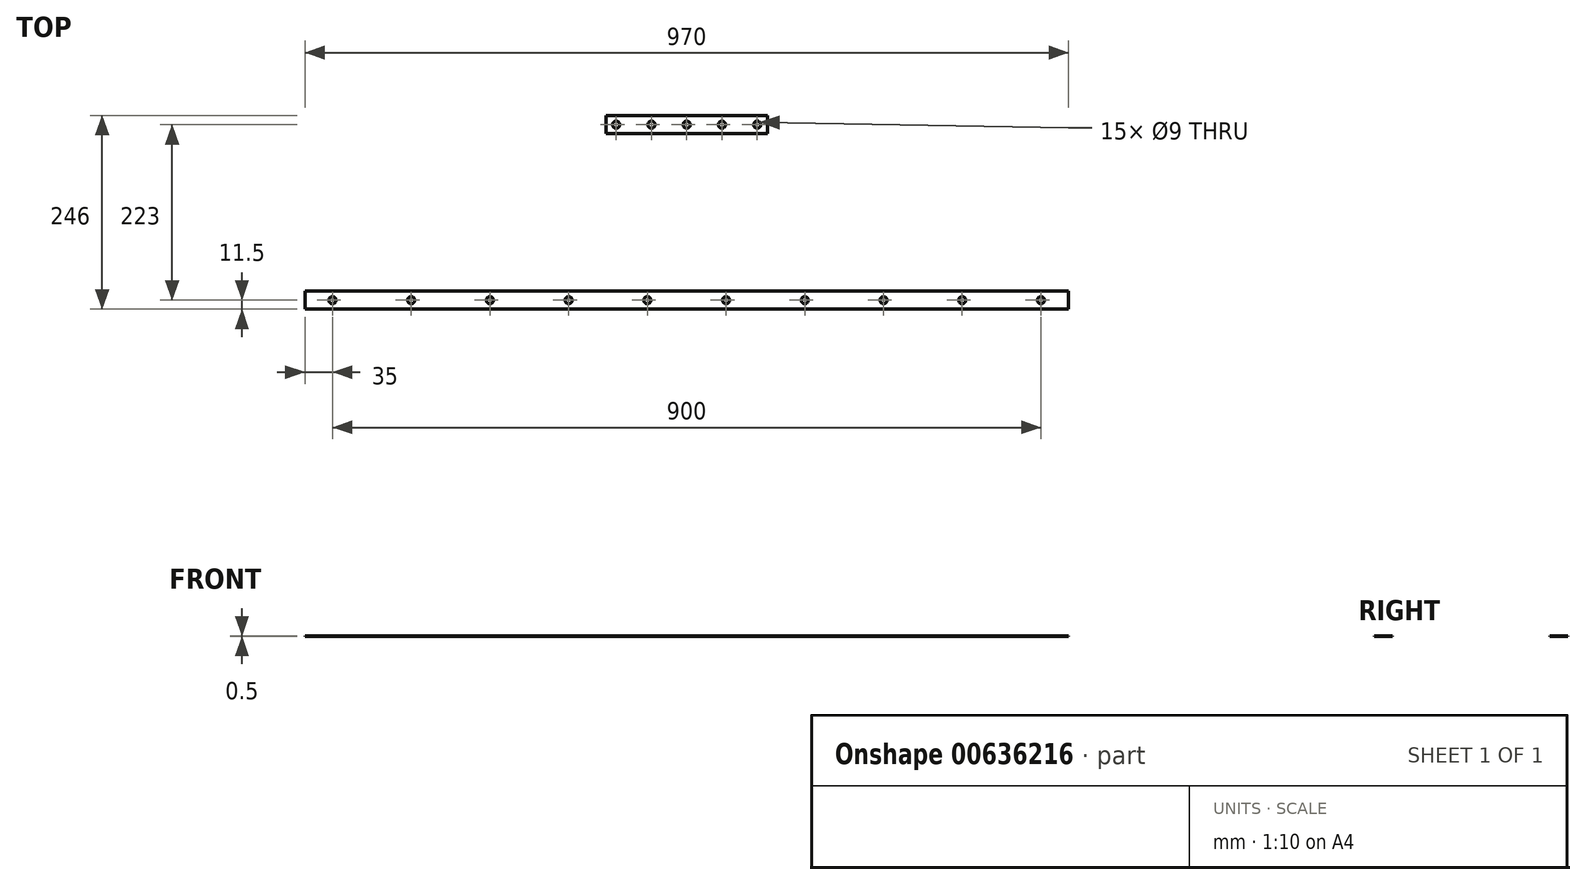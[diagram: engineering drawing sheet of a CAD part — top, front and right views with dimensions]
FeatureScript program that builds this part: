
annotation { "Feature Type Name" : "Feature", "Feature Type Description" : "" }
export const myFeature = defineFeature(function(context is Context, id is Id, definition is map)
    precondition{}
    {
        {
            var Q0;
            Q0=qCreatedBy(makeId("Top.planeOp"),FACE);
            var sketch = newSketch(context, id + "F0", { "sketchPlane" : qUnion([Q0])});
            skLineSegment(sketch, "E0.bottom", {"start": v(-485, -123) * mm, "end": v(485, -123) * mm});
            skLineSegment(sketch, "E0.top", {"start": v(-485, -100) * mm, "end": v(485, -100) * mm});
            skLineSegment(sketch, "E0.left", {"start": v(-485, -123) * mm, "end": v(-485, -100) * mm});
            skLineSegment(sketch, "E0.right", {"start": v(485, -123) * mm, "end": v(485, -100) * mm});
            skLineSegment(sketch, "E1.bottom", {"start": v(-102.5, 123) * mm, "end": v(102.5, 123) * mm});
            skLineSegment(sketch, "E1.top", {"start": v(-102.5, 100) * mm, "end": v(102.5, 100) * mm});
            skLineSegment(sketch, "E1.left", {"start": v(-102.5, 123) * mm, "end": v(-102.5, 100) * mm});
            skLineSegment(sketch, "E1.right", {"start": v(102.5, 123) * mm, "end": v(102.5, 100) * mm});
            skCircle(sketch, "E2", {"center": v(0, 111.5) * mm, "radius": 4.5 * mm});
            skLineSegment(sketch, "E3", {"start": v(-114.98, 111.5) * mm, "end": v(117, 111.5) * mm, "construction": true});
            skCircle(sketch, "E4", {"center": v(-44.8, 111.5) * mm, "radius": 4.5 * mm});
            skCircle(sketch, "E5", {"center": v(-89.6, 111.5) * mm, "radius": 4.5 * mm});
            skCircle(sketch, "E6", {"center": v(44.8, 111.5) * mm, "radius": 4.5 * mm});
            skCircle(sketch, "E7", {"center": v(89.6, 111.5) * mm, "radius": 4.5 * mm});
            skLineSegment(sketch, "E8", {"start": v(-468.3, -111.5) * mm, "end": v(492.6, -111.5) * mm, "construction": true});
            skCircle(sketch, "E9", {"center": v(-50, -111.5) * mm, "radius": 4.5 * mm});
            skCircle(sketch, "E10.1.0.0", {"center": v(-150, -111.5) * mm, "radius": 4.5 * mm});
            skCircle(sketch, "E10.2.0.0", {"center": v(-250, -111.5) * mm, "radius": 4.5 * mm});
            skCircle(sketch, "E10.3.0.0", {"center": v(-350, -111.5) * mm, "radius": 4.5 * mm});
            skLineSegment(sketch, "E10.direction1", {"start": v(-50, -111.5) * mm, "end": v(-150, -111.5) * mm, "construction": true});
            skCircle(sketch, "E11.0.4.0", {"center": v(-450, -111.5) * mm, "radius": 4.5 * mm});
            skCircle(sketch, "E12.1.0.0", {"center": v(50, -111.5) * mm, "radius": 4.5 * mm});
            skCircle(sketch, "E12.2.0.0", {"center": v(150, -111.5) * mm, "radius": 4.5 * mm});
            skLineSegment(sketch, "E12.direction1", {"start": v(-50, -111.5) * mm, "end": v(50, -111.5) * mm, "construction": true});
            skCircle(sketch, "E13.0.3.0", {"center": v(250, -111.5) * mm, "radius": 4.5 * mm});
            skCircle(sketch, "E13.0.4.0", {"center": v(350, -111.5) * mm, "radius": 4.5 * mm});
            skCircle(sketch, "E13.0.5.0", {"center": v(450, -111.5) * mm, "radius": 4.5 * mm});
            skSolve(sketch);
        }
        {
            var Q0;
            Q0=makeQuery(id+"F0.imprint","IMPRINT",FACE,{"disambiguationData":[TD([[makeQuery(id+"F0.imprint","IMPRINT",EDGE,{"derivedFrom":sQuery(id+"F0.wireOp",EDGE,"E1.bottom")}),-1.0]])]});
            var Q1;
            Q1=makeQuery(id+"F0.imprint","IMPRINT",FACE,{"disambiguationData":[TD([[makeQuery(id+"F0.imprint","IMPRINT",EDGE,{"derivedFrom":sQuery(id+"F0.wireOp",EDGE,"E0.bottom")}),1.0]])]});
            extrude(context, id + "F1", {"entities" : qUnion([Q0, Q1]), "depth" : 0.5 * mm, "offsetDistance" : 25 * mm});
        }
    });
